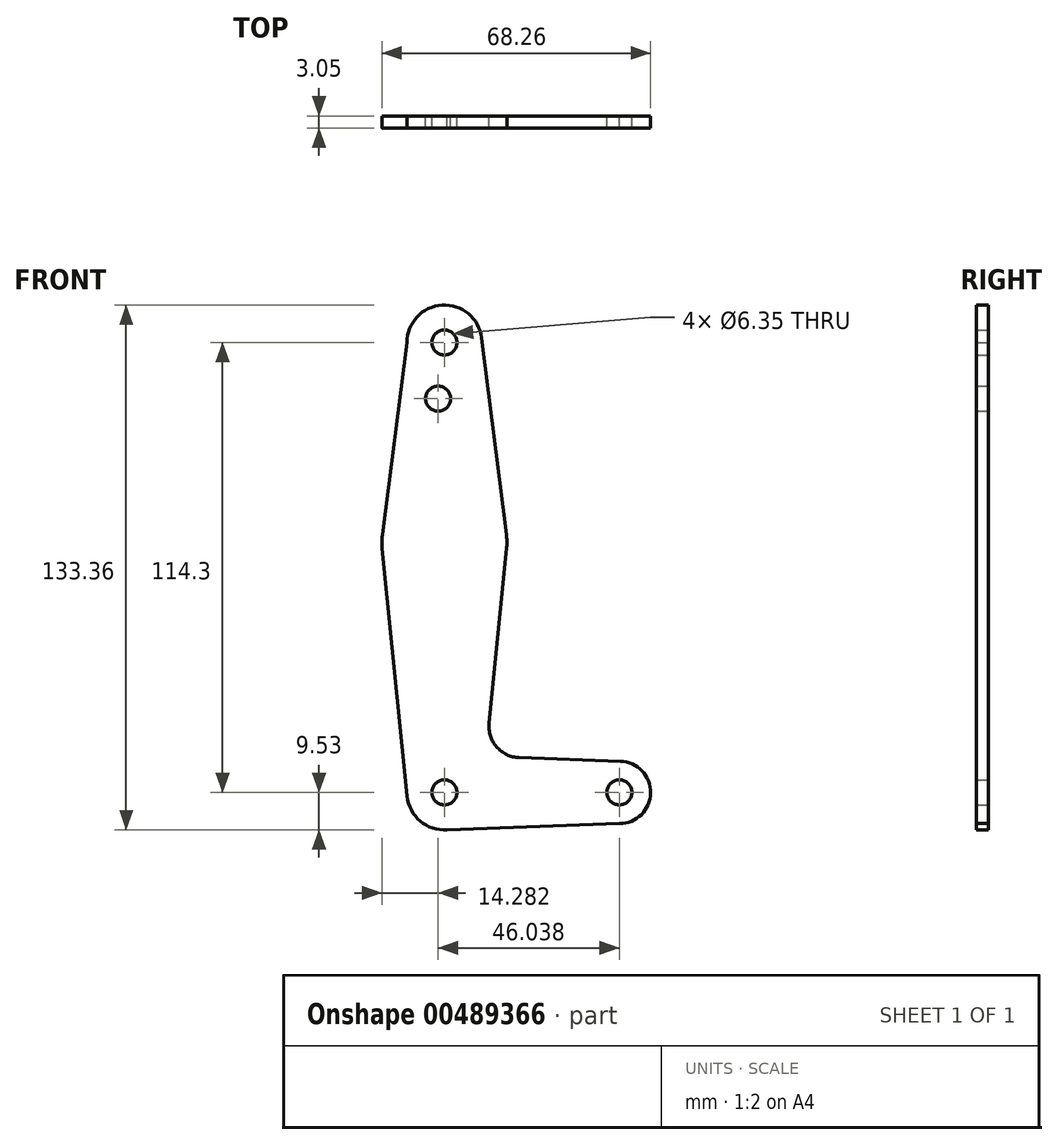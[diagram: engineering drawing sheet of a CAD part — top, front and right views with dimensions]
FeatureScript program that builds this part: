
annotation { "Feature Type Name" : "Feature", "Feature Type Description" : "" }
export const myFeature = defineFeature(function(context is Context, id is Id, definition is map)
    precondition{}
    {
        {
            var Q0;
            Q0=qCreatedBy(makeId("Front.planeOp"),FACE);
            var sketch = newSketch(context, id + "F0", { "sketchPlane" : qUnion([Q0])});
            skLineSegment(sketch, "E0", {"start": v(0, 0) * mm, "end": v(0, 114.3) * mm, "construction": true});
            skLineSegment(sketch, "E1", {"start": v(0, 0) * mm, "end": v(44.45, 0) * mm, "construction": true});
            skCircle(sketch, "E2", {"center": v(0, 114.3) * mm, "radius": 9.52 * mm});
            skCircle(sketch, "E3", {"center": v(0, 0) * mm, "radius": 9.53 * mm});
            skCircle(sketch, "E4", {"center": v(44.45, 0) * mm, "radius": 7.94 * mm});
            skCircle(sketch, "E5", {"center": v(0, 63.5) * mm, "radius": 15.88 * mm});
            skLineSegment(sketch, "E6", {"start": v(18.97, 8.85) * mm, "end": v(44.73, 7.93) * mm});
            skLineSegment(sketch, "E7", {"start": v(0, -9.52) * mm, "end": v(44.45, -7.94) * mm});
            skLineSegment(sketch, "E8", {"start": v(9.45, 115.5) * mm, "end": v(15.75, 65.48) * mm});
            skLineSegment(sketch, "E9", {"start": v(-9.52, 114.3) * mm, "end": v(-15.75, 65.5) * mm});
            skLineSegment(sketch, "E10", {"start": v(-15.8, 61.91) * mm, "end": v(-9.48, -0.95) * mm});
            skLineSegment(sketch, "E11", {"start": v(15.8, 61.91) * mm, "end": v(11.34, 17.59) * mm});
            skCircle(sketch, "E12", {"center": v(0, 114.3) * mm, "radius": 3.18 * mm});
            skCircle(sketch, "E13", {"center": v(0, 0) * mm, "radius": 3.18 * mm});
            skCircle(sketch, "E14", {"center": v(44.45, 0) * mm, "radius": 3.18 * mm});
            skCircle(sketch, "E15", {"center": v(-1.59, 100.03) * mm, "radius": 3.18 * mm});
            skArc(sketch, "E16.filletArc", {"start": v(11.34, 17.59) * mm, "mid": v(13.26, 11.57) * mm, "end": v(18.97, 8.85) * mm});
            skSolve(sketch);
        }
        {
            var Q0;
            Q0 = qSketchRegion(id + "F0", true);
            extrude(context, id + "F1", {"entities" : qUnion([Q0]), "depth" : 3.05 * mm});
        }
    });
